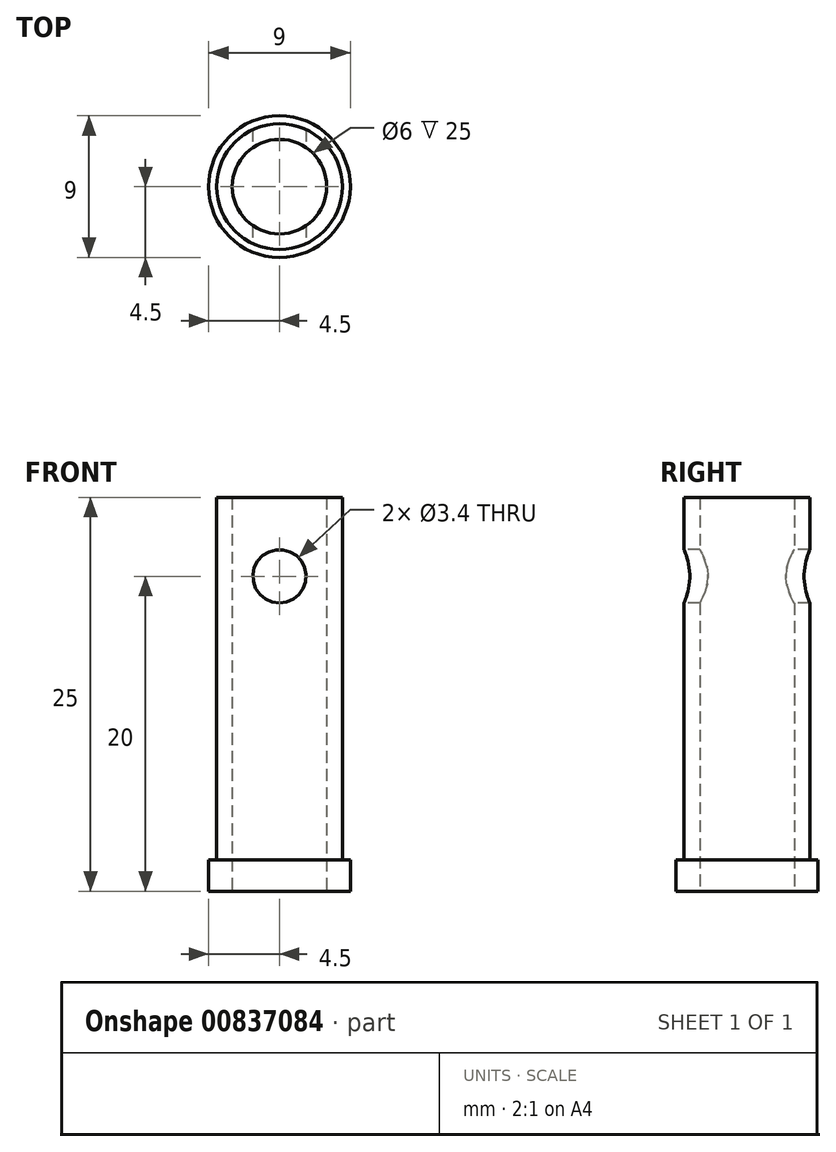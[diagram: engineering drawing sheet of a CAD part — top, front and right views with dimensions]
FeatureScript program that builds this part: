
annotation { "Feature Type Name" : "Feature", "Feature Type Description" : "" }
export const myFeature = defineFeature(function(context is Context, id is Id, definition is map)
    precondition{}
    {
        {
            var Q0;
            Q0=qCreatedBy(makeId("Top.planeOp"),FACE);
            var sketch = newSketch(context, id + "F0", { "sketchPlane" : qUnion([Q0])});
            skCircle(sketch, "E0", {"center": v(0, 0) * mm, "radius": 3 * mm});
            skCircle(sketch, "E1", {"center": v(0, 0) * mm, "radius": 4 * mm});
            skCircle(sketch, "E2", {"center": v(0, 0) * mm, "radius": 4.5 * mm});
            skSolve(sketch);
        }
        {
            var Q0;
            Q0=makeQuery(id+"F0.imprint","IMPRINT",FACE,{"disambiguationData":[TD([[makeQuery(id+"F0.imprint","IMPRINT",EDGE,{"derivedFrom":sQuery(id+"F0.wireOp",EDGE,"E0")}),-1.0]])]});
            extrude(context, id + "F1", {"entities" : qUnion([Q0]), "depth" : 25 * mm, "offsetDistance" : 25 * mm});
        }
        {
            var Q0;
            Q0 = qSketchRegion(id + "F0", true);
            extrude(context, id + "F2", {"entities" : qUnion([Q0]), "operationType" : NewBodyOperationType.ADD, "depth" : 2 * mm, "offsetDistance" : 25 * mm});
        }
        {
            var Q0;
            Q0=qCreatedBy(makeId("Front.planeOp"),FACE);
            cPlane(context, id + "F3", {"entities" : qUnion([Q0]), "cplaneType" : CPlaneType.OFFSET, "offset" : 4 * mm, "width" : 150 * mm, "height" : 150 * mm});
        }
        {
            var Q0;
            Q0=qCreatedBy(id+"F3.planeOp",FACE);
            var sketch = newSketch(context, id + "F4", { "sketchPlane" : qUnion([Q0])});
            skLineSegment(sketch, "E3", {"start": v(0, 0) * mm, "end": v(0, 23) * mm, "construction": true});
            skLineSegment(sketch, "E4", {"start": v(-15.4, 20) * mm, "end": v(13.32, 20) * mm, "construction": true});
            skCircle(sketch, "E5", {"center": v(0, 20) * mm, "radius": 1.5 * mm});
            skSolve(sketch);
        }
        {
            var Q0;
            Q0=sQuery(id+"F4.wireOp",VERTEX,"E5.center");
            var Q1;
            Q1=makeQuery(id+"F1.opExtrude","SWEPT_BODY",BODY,{"disambiguationData":[OSD([sQuery(id+"F0.wireOp",EDGE,"E0"),sQuery(id+"F0.wireOp",EDGE,"E1")])]});
            hole(context, id + "F5", {"style" : HoleStyle.SIMPLE, "endStyle" : HoleEndStyle.THROUGH, "standardTappedOrClearance" : lookupTablePath({ "fit" : "Normal", "standard" : "ISO", "size" : "M3", "type" : "Clearance" }), "standardBlindInLast" : lookupTablePath({ "fit" : "Normal", "standard" : "ISO", "engagement" : "75%", "pitch" : "0.5 mm", "size" : "M3", "type" : "Clearance & tapped" }), "holeDiameter" : 3.4 * mm, "majorDiameter" : 5 * mm, "isTappedThrough" : true, "tappedDepth" : 12 * mm, "tapClearance" : 3, "startFromSketch" : true, "locations" : qUnion([Q0]), "scope" : qUnion([Q1])});
        }
    });
